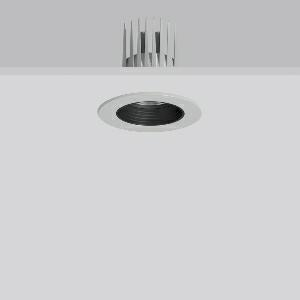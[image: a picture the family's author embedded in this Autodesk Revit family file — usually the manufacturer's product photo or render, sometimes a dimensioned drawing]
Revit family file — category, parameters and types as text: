
# Revit family: heledon_mini_e_901747_004_1_0711
name_source: partatom
category: Lighting Fixtures
units: mm (PartAtom-declared; Revit-internal decimal feet)

## family parameters
Cut with Voids When Loaded = No
Host = Face
Light Source = No
Part Type = Normal
Room Calculation Point = No
Round Connector Dimension = Use Diameter
Shared = No

## types (1)
- HELEDON mini E (1 x LED Modul 940, 2050 lm, 4000)
    Apparent Load = 20 VA
    Approval mark = CE
    CIE Flux Codes = 95 100 100 100 100
    Color Rendering = 92
    Color Temperature = 4000
    Default Elevation = 1800 mm
    Description = Series: HELEDON mini
Round recessed downlight. Housing: die-cast aluminium, powder-coated. Black plastic ring and recessed LED to prevent glare from the side. Optical assembly with lens made of plastic (polycarbonate) for the best homogeneous light distribution - can be changed without tools. Best colour rendering index Ra>90. Suitable for Recessed ceiling mounting. Installation without tools thanks to spring fastening system. Including separate LED converter with connecting cable 600 mm.High quality converter without flickering and stroboscopic effect. Through-wiring box (5 pole) available as accessory. The following accessories can be mounted without use of tools: interchangeable lenses, decorative glasses, honeycomb louvre, clear and frosted diffusers, white interchangeable plastic ring. 
Colour: silver
Diameter: 124 mm
Height: 3 mm
Cut-out diameter: 114 mm
Recess height: 170 mm
Luminaire: recess height: 120 mm
Lamp: LED
Socket: without socket
Colour temperature: 4000K
Colour rendering index (CRI): 92
System power: 20 W
Rated luminous flux: 2050 lm
Luminous efficiency: 103 lm/W
Control gear: Regulated power supply
Protection class: II
Type of protection: IP 20
    Height = 0 mm  [stored 0 ft]
    Lamp = 1 x LED Modul 940
    Lamp Light Flux = 2050 lm
    Lamp count = 1
    Length = 124 mm  [stored 0.406824 ft]
    Lifetime = 50000 h
    Luminous efficacy = 103 lm/W
    Manufacturer = RZB
    ModVariant = No
    Model = 901747.004.1
    Mounting Place = Ceiling
    Mounting Type = Recessed
    Number of Poles = 1
    OnlyDefault = Yes
    Power Factor = 1
    Product Name = HELEDON mini E
    Product group = Recessed downlights
    ProductGroupID = 402
    Protection Class = Protection class II
    Protection Degree = IP 20
    RLX_Detail_Level = 1
    RLX_Emergency_Light_Flux = 0 lm
    RLX_Emergency_Type = 0
    RLX_Emergency_Type_DB = No
    RlxData = <blob elided: 133577 chars, md5=aba8999a>
    Socket = socket
    Standby Power = 0 W
    System Light Flux = 2050 lm
    System Power = 20 W
    Type Comments = Product without accessories
    Type Image = 901656.004.jpg
    URL = http://relux.com
    VarID = ---
    Voltage = 230 V
    Voltage Range = 220-240 V
    Weight = 0.00 kg
    Width = 0 mm  [stored 0 ft]

note: [stored X ft] marks values corroborated as IEEE doubles in the binary element streams (Revit-internal decimal feet)

## geometry (parser evidence)
native form markers: Blend x4, Sweep x10
no freeform markers — native parametric forms only
